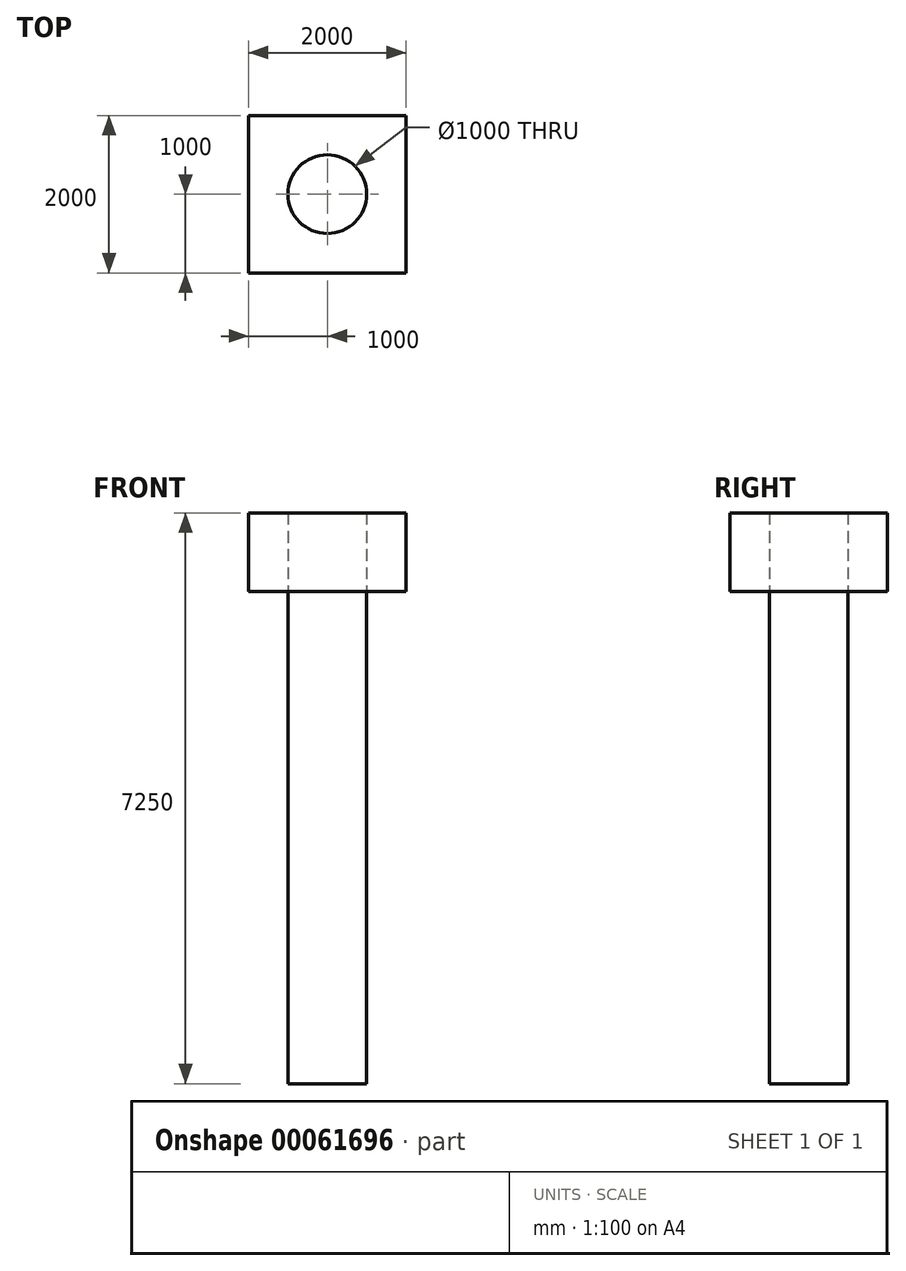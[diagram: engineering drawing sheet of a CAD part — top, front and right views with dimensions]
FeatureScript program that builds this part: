
annotation { "Feature Type Name" : "Feature", "Feature Type Description" : "" }
export const myFeature = defineFeature(function(context is Context, id is Id, definition is map)
    precondition{}
    {
        {
            var Q0;
            Q0=qCreatedBy(makeId("Top.planeOp"),FACE);
            var sketch = newSketch(context, id + "F0", { "sketchPlane" : qUnion([Q0])});
            skCircle(sketch, "E0", {"center": v(0, 0) * mm, "radius": 500 * mm});
            skSolve(sketch);
        }
        {
            var Q0;
            Q0=makeQuery(id+"F0.imprint","IMPRINT",FACE,{"disambiguationData":[TD([[makeQuery(id+"F0.imprint","IMPRINT",EDGE,{"derivedFrom":sQuery(id+"F0.wireOp",EDGE,"E0")}),1.0]])]});
            extrude(context, id + "F1", {"entities" : qUnion([Q0]), "depth" : 4250 * mm});
        }
        {
            var Q0;
            Q0=makeQuery(id+"F1.opExtrude","CAP_FACE",FACE,{"disambiguationData":[OSD([sQuery(id+"F0.wireOp",EDGE,"E0")])],"isStart":false});
            var sketch = newSketch(context, id + "F2", { "sketchPlane" : qUnion([Q0])});
            skLineSegment(sketch, "E1.rect.bottom", {"start": v(1000, 1000) * mm, "end": v(-1000, 1000) * mm});
            skLineSegment(sketch, "E1.rect.top", {"start": v(1000, -1000) * mm, "end": v(-1000, -1000) * mm});
            skLineSegment(sketch, "E1.rect.left", {"start": v(1000, 1000) * mm, "end": v(1000, -1000) * mm});
            skLineSegment(sketch, "E1.rect.right", {"start": v(-1000, 1000) * mm, "end": v(-1000, -1000) * mm});
            skPoint(sketch, "E1.rect.middle", {"position": v(0, 0) * mm});
            skSolve(sketch);
        }
        {
            var Q0;
            Q0=makeQuery(id+"F2.imprint","IMPRINT",FACE,{"disambiguationData":[TD([[makeQuery(id+"F2.imprint","IMPRINT",EDGE,{"derivedFrom":sQuery(id+"F2.wireOp",EDGE,"E1.rect.bottom")}),1.0]])]});
            extrude(context, id + "F3", {"entities" : qUnion([Q0]), "depth" : 1000 * mm});
        }
        {
            var Q0;
            Q0=makeQuery(id+"F1.opExtrude","CAP_FACE",FACE,{"disambiguationData":[OSD([sQuery(id+"F0.wireOp",EDGE,"E0")])],"isStart":true});
            extrude(context, id + "F4", {"entities" : qUnion([Q0]), "operationType" : NewBodyOperationType.ADD, "depth" : 2000 * mm});
        }
    });
